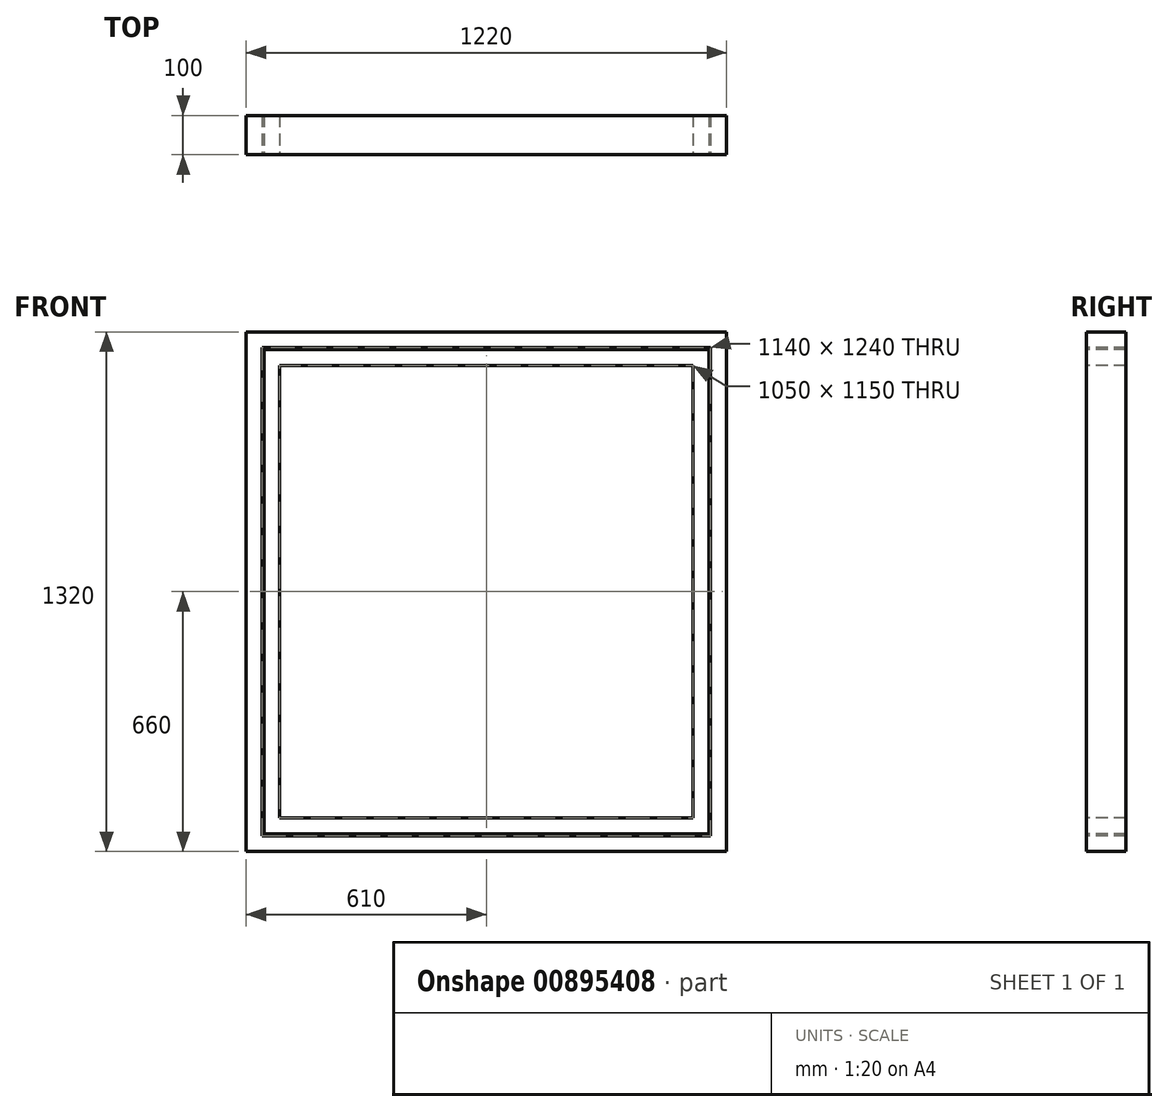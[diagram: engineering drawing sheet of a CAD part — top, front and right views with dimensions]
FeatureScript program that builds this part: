
annotation { "Feature Type Name" : "Feature", "Feature Type Description" : "" }
export const myFeature = defineFeature(function(context is Context, id is Id, definition is map)
    precondition{}
    {
        {
            var Q0;
            Q0=qCreatedBy(makeId("Front.planeOp"),FACE);
            cPlane(context, id + "F0", {"entities" : qUnion([Q0]), "cplaneType" : CPlaneType.OFFSET, "offset" : 150 * mm, "oppositeDirection" : true, "width" : 150 * mm, "height" : 150 * mm});
        }
        {
            var Q0;
            Q0=qCreatedBy(id+"F0.planeOp",FACE);
            var sketch = newSketch(context, id + "F1", { "sketchPlane" : qUnion([Q0])});
            skLineSegment(sketch, "E0.bottom", {"start": v(610, -660) * mm, "end": v(-610, -660) * mm});
            skLineSegment(sketch, "E0.top", {"start": v(610, 660) * mm, "end": v(-610, 660) * mm});
            skLineSegment(sketch, "E0.left", {"start": v(610, -660) * mm, "end": v(610, 660) * mm});
            skLineSegment(sketch, "E0.right", {"start": v(-610, -660) * mm, "end": v(-610, 660) * mm});
            skPoint(sketch, "E0.middle", {"position": v(0, 0) * mm});
            skLineSegment(sketch, "E1.bottom", {"start": v(570, -620) * mm, "end": v(-570, -620) * mm});
            skLineSegment(sketch, "E1.top", {"start": v(570, 620) * mm, "end": v(-570, 620) * mm});
            skLineSegment(sketch, "E1.left", {"start": v(570, -620) * mm, "end": v(570, 620) * mm});
            skLineSegment(sketch, "E1.right", {"start": v(-570, -620) * mm, "end": v(-570, 620) * mm});
            skLineSegment(sketch, "E2.bottom", {"start": v(565, -615) * mm, "end": v(-565, -615) * mm});
            skLineSegment(sketch, "E2.top", {"start": v(565, 615) * mm, "end": v(-565, 615) * mm});
            skLineSegment(sketch, "E2.left", {"start": v(565, -615) * mm, "end": v(565, 615) * mm});
            skLineSegment(sketch, "E2.right", {"start": v(-565, -615) * mm, "end": v(-565, 615) * mm});
            skLineSegment(sketch, "E3.bottom", {"start": v(525, -575) * mm, "end": v(-525, -575) * mm});
            skLineSegment(sketch, "E3.top", {"start": v(525, 575) * mm, "end": v(-525, 575) * mm});
            skLineSegment(sketch, "E3.left", {"start": v(525, -575) * mm, "end": v(525, 575) * mm});
            skLineSegment(sketch, "E3.right", {"start": v(-525, -575) * mm, "end": v(-525, 575) * mm});
            skSolve(sketch);
        }
        {
            var Q0;
            Q0=makeQuery(id+"F1.imprint","IMPRINT",FACE,{"disambiguationData":[TD([[makeQuery(id+"F1.imprint","IMPRINT",EDGE,{"derivedFrom":sQuery(id+"F1.wireOp",EDGE,"E2.bottom")}),-1.0]])]});
            var Q1;
            Q1=makeQuery(id+"F1.imprint","IMPRINT",FACE,{"disambiguationData":[TD([[makeQuery(id+"F1.imprint","IMPRINT",EDGE,{"derivedFrom":sQuery(id+"F1.wireOp",EDGE,"E0.bottom")}),-1.0]])]});
            extrude(context, id + "F2", {"entities" : qUnion([Q0, Q1]), "oppositeDirection" : true, "depth" : 100 * mm, "offsetDistance" : 25 * mm});
        }
    });
